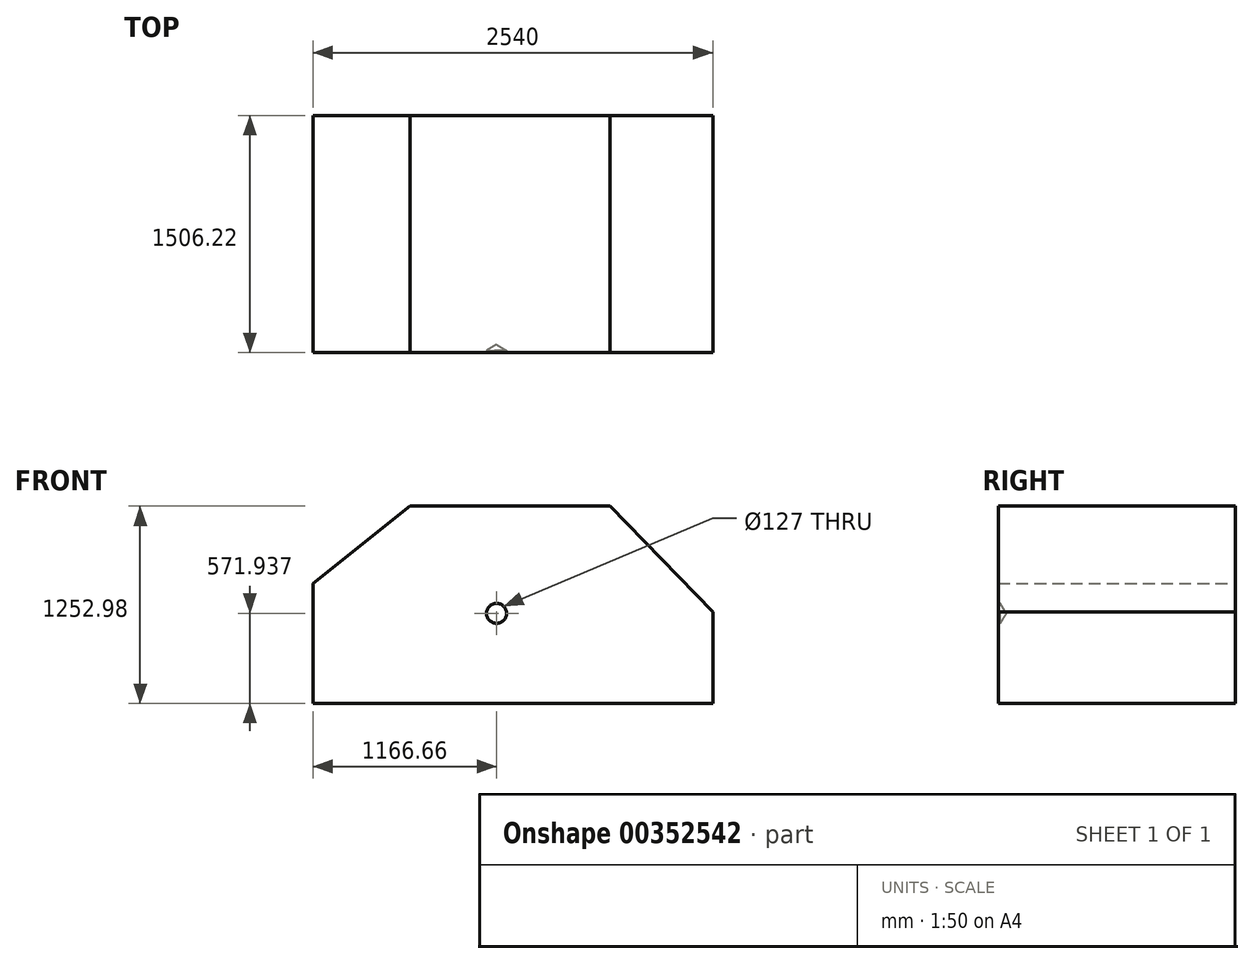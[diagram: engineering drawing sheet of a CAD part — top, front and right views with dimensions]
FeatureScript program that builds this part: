
annotation { "Feature Type Name" : "Feature", "Feature Type Description" : "" }
export const myFeature = defineFeature(function(context is Context, id is Id, definition is map)
    precondition{}
    {
        {
            var Q0;
            Q0=qCreatedBy(makeId("Front.planeOp"),FACE);
            var sketch = newSketch(context, id + "F0", { "sketchPlane" : qUnion([Q0])});
            skLineSegment(sketch, "E0", {"start": v(-1387.31, 123) * mm, "end": v(-770.64, 613.97) * mm});
            skLineSegment(sketch, "E1", {"start": v(-770.64, 613.97) * mm, "end": v(499.36, 613.97) * mm});
            skLineSegment(sketch, "E2", {"start": v(499.36, 613.97) * mm, "end": v(1152.69, -57.69) * mm});
            skLineSegment(sketch, "E3", {"start": v(1152.69, -57.69) * mm, "end": v(1152.69, -639) * mm});
            skLineSegment(sketch, "E4", {"start": v(1152.69, -639) * mm, "end": v(-1387.31, -639) * mm});
            skLineSegment(sketch, "E5", {"start": v(-1387.31, -639) * mm, "end": v(-1387.31, 123) * mm});
            skSolve(sketch);
        }
        {
            var Q0;
            Q0 = qSketchRegion(id + "F0", true);
            extrude(context, id + "F1", {"entities" : qUnion([Q0]), "depth" : 1506.22 * mm});
        }
        {
            var Q0;
            Q0=makeQuery(id+"F1.opExtrude","CAP_FACE",FACE,{"disambiguationData":[OSD([sQuery(id+"F0.wireOp",EDGE,"E0"),sQuery(id+"F0.wireOp",EDGE,"E1"),sQuery(id+"F0.wireOp",EDGE,"E2"),sQuery(id+"F0.wireOp",EDGE,"E3"),sQuery(id+"F0.wireOp",EDGE,"E4"),sQuery(id+"F0.wireOp",EDGE,"E5")])],"isStart":false});
            var sketch = newSketch(context, id + "F2", { "sketchPlane" : qUnion([Q0])});
            skCircle(sketch, "E6", {"center": v(-220.64, -67.07) * mm, "radius": 307.08 * mm});
            skSolve(sketch);
        }
        {
            var Q0;
            Q0=sQuery(id+"F2.wireOp",VERTEX,"E6.center");
            var Q1;
            Q1=makeQuery(id+"F1.opExtrude","SWEPT_BODY",BODY,{"disambiguationData":[OSD([sQuery(id+"F0.wireOp",EDGE,"E0"),sQuery(id+"F0.wireOp",EDGE,"E1"),sQuery(id+"F0.wireOp",EDGE,"E2"),sQuery(id+"F0.wireOp",EDGE,"E3"),sQuery(id+"F0.wireOp",EDGE,"E4"),sQuery(id+"F0.wireOp",EDGE,"E5")])]});
            hole(context, id + "F3", {"style" : HoleStyle.SIMPLE, "endStyle" : HoleEndStyle.BLIND, "holeDiameter" : 127 * mm, "holeDepth" : 12.7 * mm, "isTappedThrough" : true, "tappedDepth" : 12.7 * mm, "tapClearance" : 3, "locations" : qUnion([Q0]), "scope" : qUnion([Q1])});
        }
    });
